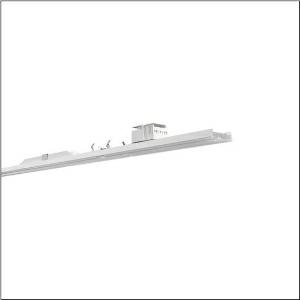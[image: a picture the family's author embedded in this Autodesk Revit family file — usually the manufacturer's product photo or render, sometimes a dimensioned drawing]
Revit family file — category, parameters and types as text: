
# Revit family: licross_r__11_recessed_ho_51tl12dn5dxl_9b20
name_source: partatom
category: Lighting Fixtures
units: mm (PartAtom-declared; Revit-internal decimal feet)

## family parameters
Cut with Voids When Loaded = No
Host = Face
Light Source = No
Part Type = Normal
Room Calculation Point = No
Round Connector Dimension = Use Diameter
Shared = No

## types (1)
- --- (1 x LED, 13030 lm, 76 W, 5000K)
    Apparent Load = 76 VA
    CIE Flux Codes = 66 91 98 100 100
    Color Rendering = 80
    Color Temperature = 5000K
    Default Elevation = 1800 mm
    Description = Licross® 11 Recessed HOluminaire insert, length: 1.500mm, width: 66mm, height: 67mm, LED rated luminous flux: 13.030lm, light colour: 850, control gear: DALI 2, control gear: ECG DALI, with plug, 5-pole, with phase selection, mains connection: 220..240V, AC, 50/60Hz, halogen-free wiring, primary optical cover: cover, of PMMA, light emission: direct distribution, protection rating (complete): IP40, insulation class (complete): insulation class I (protective earthing), certification: CE, ENEC, VDE, protection symbol: D if used in an environment without relevant dust loads with corresponding accessories, permissible ambient temperature for indoor applications: -25..+35°C, reducing of maximum allowable ambient temperature of 5°C with ceiling mounting, corresponds to IFS (International Featured Standards) requirements for safety and quality in the food industry, packaging unit: 1 piece
    Height = 58 mm
    Lamp = 1 x LED
    Lamp Light Flux = 13030 lm
    Lamp Power = 76 W
    Lamp count = 1
    Length = 1500 mm
    Luminous efficacy = 171 lm/W
    Manufacturer = Siteco
    ModVariant = No
    Model = 51TL12DN5DXL
    Mounting Place = Ceiling
    Mounting Type = Pendant
    Number of Poles = 1
    OnlyDefault = Yes
    Power Factor = 1
    Product Name = Licross® 11 Recessed HO
    Product group = luminaire insert
    ProductGroupID = 902
    Protection Class = Protection class I
    Protection Degree = IP 40
    RLX_Detail_Level = 1
    RlxData = <blob elided: 22169 chars, md5=22bb07c2>
    Socket = socket
    Standby Power = 0 W
    System Light Flux = 13030 lm
    System Power = 76 W
    Type Comments = factory setting: luminous flux: 100 % | dim-lin: 254 | 430 mA
    Type Image = l_1266722.jpg
    URL = http://relux.com
    VarID = @adj_139113
    Voltage = 0 V
    Weight = 0.00 kg
    Width = 66 mm

## geometry (parser evidence)
native form markers: Blend x4, Sweep x10
no freeform markers — native parametric forms only
